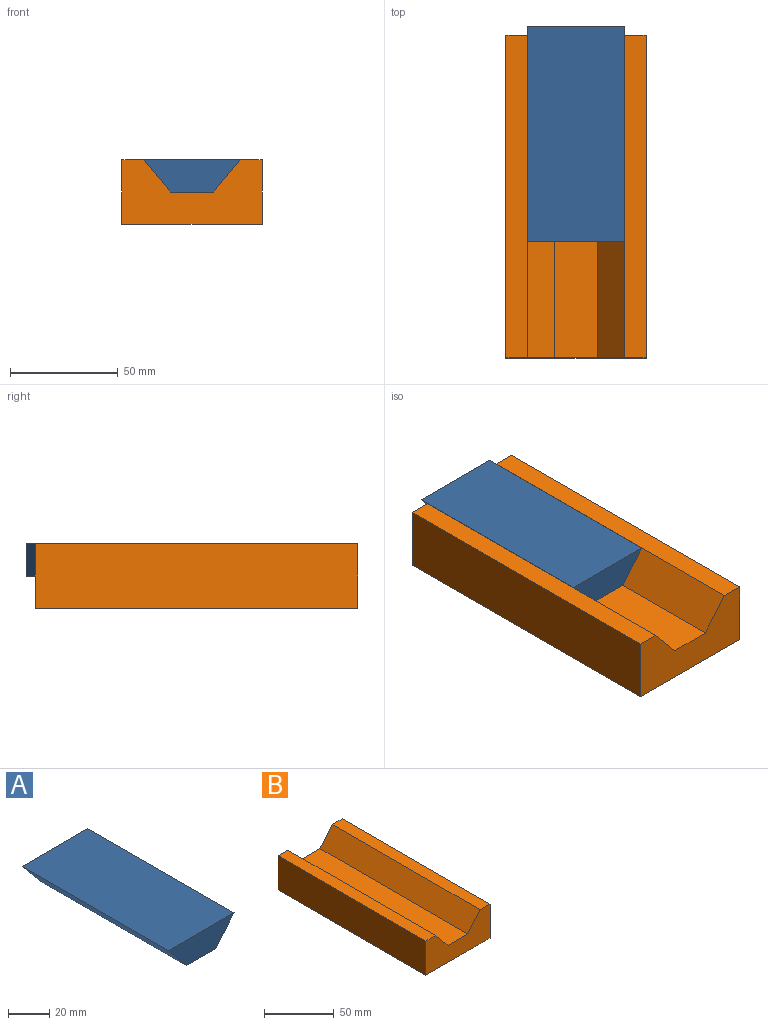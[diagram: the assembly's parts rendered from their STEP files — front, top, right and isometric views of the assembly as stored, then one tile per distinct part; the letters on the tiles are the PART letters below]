
ASSEMBLY  parts=2 mates=1
PART A: 6 faces, bbox 45.2x100x15 mm
  f0: plane 100x15mm, normal (-0.77,0,-0.64), area 1958.1mm2, adj f1,f3,f4,f5
  f1: plane 100x20mm, normal (0,0,-1), area 2000mm2, adj f0,f2,f4,f5
  f2: plane 100x15mm, normal (0.77,0,-0.64), area 1958.1mm2, adj f1,f3,f4,f5
  f3: plane 100x45.17mm, normal (0,0,1), area 4517.3mm2, adj f0,f2,f4,f5
  f4: plane 45.17x15mm, normal (0,-1,0), area 488.8mm2, adj f0,f1,f2,f3
  f5: plane 45.17x15mm, normal (0,1,0), area 488.8mm2, adj f0,f1,f2,f3
PART B: 10 faces, bbox 65.2x150x30 mm
  f0: plane 150x30mm, normal (-1,0,0), area 4500mm2, adj f1,f7,f8,f9
  f1: plane 150x65.17mm, normal (0,0,-1), area 9775.9mm2, adj f0,f2,f8,f9
  f2: plane 150x30mm, normal (1,0,0), area 4500mm2, adj f1,f3,f8,f9
  f3: plane 150x10mm, normal (0,0,1), area 1500mm2, adj f2,f4,f8,f9
  f4: plane 150x15mm, normal (-0.77,0,0.64), area 2937.2mm2, adj f3,f5,f8,f9
  f5: plane 150x20mm, normal (0,0,1), area 3000mm2, adj f4,f6,f8,f9
  f6: plane 150x15mm, normal (0.77,0,0.64), area 2937.2mm2, adj f5,f7,f8,f9
  f7: plane 150x10mm, normal (0,0,1), area 1500mm2, adj f0,f6,f8,f9
  f8: plane 65.17x30mm, normal (0,-1,0), area 1466.4mm2, adj f0,f1,f2,f3,f4,f5,f6,f7
  f9: plane 65.17x30mm, normal (0,1,0), area 1466.4mm2, adj f0,f1,f2,f3,f4,f5,f6,f7
PLACE A t=(-22.44,106.75,-26.19)mm
PLACE B t=(-22.44,102.4,-26.19)mm fixed
MATE slider A.f4 <-> B.f8  axis (0,-1,0) through (-22.44,6.75,-26.19)mm
